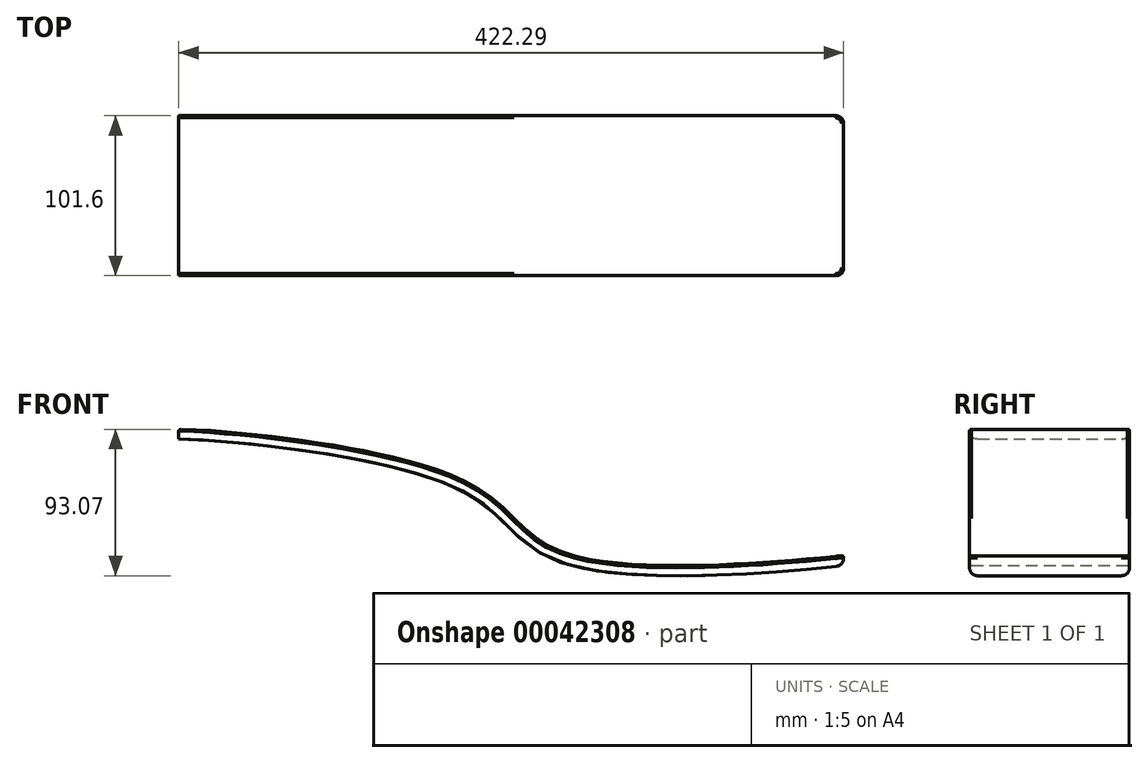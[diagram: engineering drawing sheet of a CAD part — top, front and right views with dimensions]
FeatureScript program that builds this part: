
annotation { "Feature Type Name" : "Feature", "Feature Type Description" : "" }
export const myFeature = defineFeature(function(context is Context, id is Id, definition is map)
    precondition{}
    {
        {
            var Q0;
            Q0=qCreatedBy(makeId("Front.planeOp"),FACE);
            var sketch = newSketch(context, id + "F0", { "sketchPlane" : qUnion([Q0])});
            skFitSpline(sketch, "E0", {"points": [v(-230.4, 67.73) * mm, v(-48.76, 34.82) * mm, v(14.13, -10.74) * mm, v(191.9, -12.5) * mm], "startDerivative": vector(199.84, 0) * mm, "endDerivative": vector(300.6, 29.73) * mm});
            skFitSpline(sketch, "E1.0", {"points": [v(-230.4, 61.38) * mm, v(-229.43, 61.38) * mm, v(-227.16, 61.35) * mm, v(-221.52, 61.15) * mm, v(-212.6, 60.66) * mm, v(-199.41, 59.64) * mm, v(-184.29, 58.2) * mm, v(-167.71, 56.3) * mm, v(-144.34, 53.18) * mm, v(-120.04, 49.14) * mm, v(-96.82, 44.14) * mm, v(-80.46, 39.9) * mm, v(-68.12, 36) * mm, v(-59.32, 32.64) * mm, v(-53.31, 30.03) * mm, v(-48, 27.34) * mm, v(-43.24, 24.54) * mm, v(-38.96, 21.66) * mm, v(-33.77, 17.72) * mm, v(-28.04, 12.64) * mm, v(-21.68, 6.34) * mm, v(-15.22, -0.03) * mm, v(-9.2, -5.2) * mm, v(-3.71, -9.08) * mm, v(0.8, -11.8) * mm, v(4.94, -13.89) * mm, v(8.5, -15.42) * mm, v(11.31, -16.5) * mm, v(14.26, -17.5) * mm, v(18.34, -18.73) * mm, v(23.73, -20.08) * mm, v(30.62, -21.44) * mm, v(40.32, -22.94) * mm, v(53.3, -24.27) * mm, v(69.91, -25.12) * mm, v(87.17, -25.34) * mm, v(110.52, -24.97) * mm, v(139.39, -23.5) * mm, v(170.3, -21.02) * mm, v(186.25, -19.45) * mm, v(192.52, -18.83) * mm]});
            skLineSegment(sketch, "E2", {"start": v(-230.4, 61.38) * mm, "end": v(-230.4, 67.73) * mm});
            skLineSegment(sketch, "E3", {"start": v(191.9, -12.5) * mm, "end": v(191.9, -18.89) * mm});
            skSolve(sketch);
        }
        {
            var Q0;
            Q0=makeQuery(id+"F0.imprint","IMPRINT",FACE,{"disambiguationData":[TD([[makeQuery(id+"F0.imprint","IMPRINT",EDGE,{"derivedFrom":sQuery(id+"F0.wireOp",EDGE,"E0")}),-1.0]])]});
            extrude(context, id + "F1", {"entities" : qUnion([Q0]), "depth" : 101.6 * mm});
        }
        {
            var Q0;
            Q0=makeQuery(id+"F1.opExtrude","CAP_EDGE",EDGE,{"disambiguationData":[OSD([sQuery(id+"F0.wireOp",EDGE,"E1.0")])],"isStart":false});
            var Q1;
            Q1=makeQuery(id+"F1.opExtrude","CAP_EDGE",EDGE,{"disambiguationData":[OSD([sQuery(id+"F0.wireOp",EDGE,"E1.0")])],"isStart":true});
            fillet(context, id + "F2", {"entities" : qUnion([Q0, Q1]), "radius" : 5.08 * mm, "tangentPropagation" : true, "allowEdgeOverflow" : false});
        }
        {
            var Q0;
            Q0=makeQuery(id+"F1.opExtrude","SWEPT_EDGE",EDGE,{"disambiguationData":[OSD([sQuery(id+"F0.wireOp",EDGE,"E1.0"),sQuery(id+"F0.wireOp",EDGE,"E3")])]});
            fillet(context, id + "F3", {"entities" : qUnion([Q0]), "radius" : 5.08 * mm, "tangentPropagation" : true, "allowEdgeOverflow" : false});
        }
        {
            var Q0;
            Q0=makeQuery(id+"F1.opExtrude","SWEPT_FACE",FACE,{"disambiguationData":[OSD([sQuery(id+"F0.wireOp",EDGE,"E0")])]});
            fillet(context, id + "F4", {"entities" : qUnion([Q0]), "radius" : 1.27 * mm, "tangentPropagation" : true, "allowEdgeOverflow" : false});
        }
    });
